# Revit family: Skylight-Wasco-SkyMax
name_source: partatom
category: Windows
revit_build: Autodesk Revit Architecture 2013 (Build: 20130531_2115(x64)
units: mm (PartAtom-declared; Revit-internal decimal feet)

## types (4) — shared parameters
Curb = Wood - Wasco - Douglas Firs
Curb Width = 0' - 1 1/2"
Default Elevation = 4' - 0"
Description = Large Flat Glass Unit Skylight
Finish = Aluminum - Wasco - Aged Copper
Glazing Material = Glass - Wasco - Clear
Height Constraint = 1
Manufacturer = Wasco Skylights
Product Documentation Link = http://www.wascoskylights.com
Product Page URL = http://www.wascoskylights.com
Type Comments = Maximum Length and Width for this Product is 8’
URL = http://www.wascoskylights.com

## per-type parameters (varying)
| type | C Length | C Width | Curb Height | Height | Length | Model | Width |
| GSM5252 - 49.25" x 49.25" | 4' - 1 1/4" | 4' - 1 1/4" | 0' - 3 1/2" | 0' - 5 15/16" | 4' - 0" | GSM5252 | 4' - 0" |
| GSM5276 - 49.25" x 72.5" | 6' - 0 1/2" | 4' - 1 1/4" | 0' - 3" | 0' - 5 7/16" | 6' - 0 1/2" | GSM5276 | 4' - 1 1/4" |
| GSM5296 - 49.25" x 92.5" | 7' - 8 1/2" | 4' - 1 1/4" | 0' - 3" | 0' - 5 7/16" | 7' - 8 1/2" | GSM5296 | 4' - 1 1/4" |
| GSM6060 - 58" x 58" | 4' - 10" | 4' - 10" | 0' - 3" | 0' - 5 7/16" | 4' - 10" | GSM6060 | 4' - 10" |

## geometry (parser evidence)
native form markers: Blend x10, Sweep x3
no freeform markers — native parametric forms only
